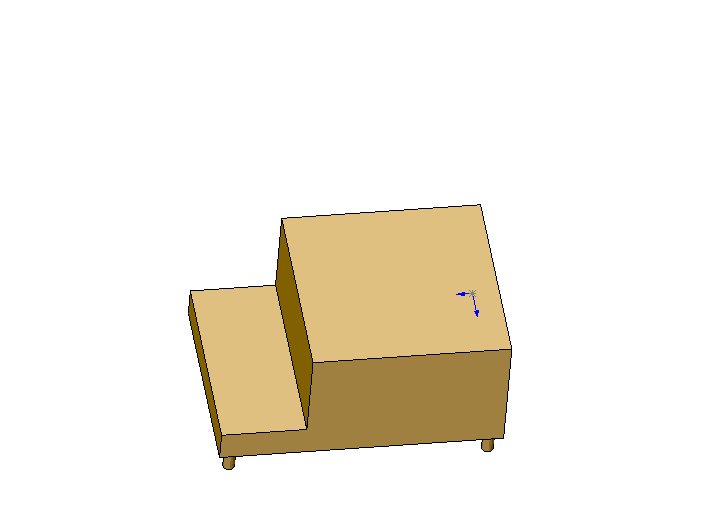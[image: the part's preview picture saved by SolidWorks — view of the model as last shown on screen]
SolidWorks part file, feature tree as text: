
SOLIDWORKS PART (.sldprt)
format: sldprt  version: not decoded by parser v0  size: 86,016 bytes
history: native  units: mm
features: sketch x3, extrude x3 (+10 scaffold rows collapsed)
feature tree (16):
  scaffold x10  (default folders/planes/origin — collapsed)
  sketch  "Sketch1"  dims[D1=114.3mm D2=80.01mm]
  extrude  "Extrude1"  Depth=12.7mm
  sketch  "Sketch2"  dims[D1=4.7625mm D2=5.08mm D3=5.08mm D4=5.08mm D5=5.08mm]
  extrude  "Extrude2"  Depth=10.16mm
  sketch  "Sketch3"  dims[D1=80.01mm]
  extrude  "Extrude3"  Depth=38.1mm
decode coverage: 6 of 6 modeling features carry decoded parameters
note: suppression state not decoded; provenance and decode notes live in map.json
